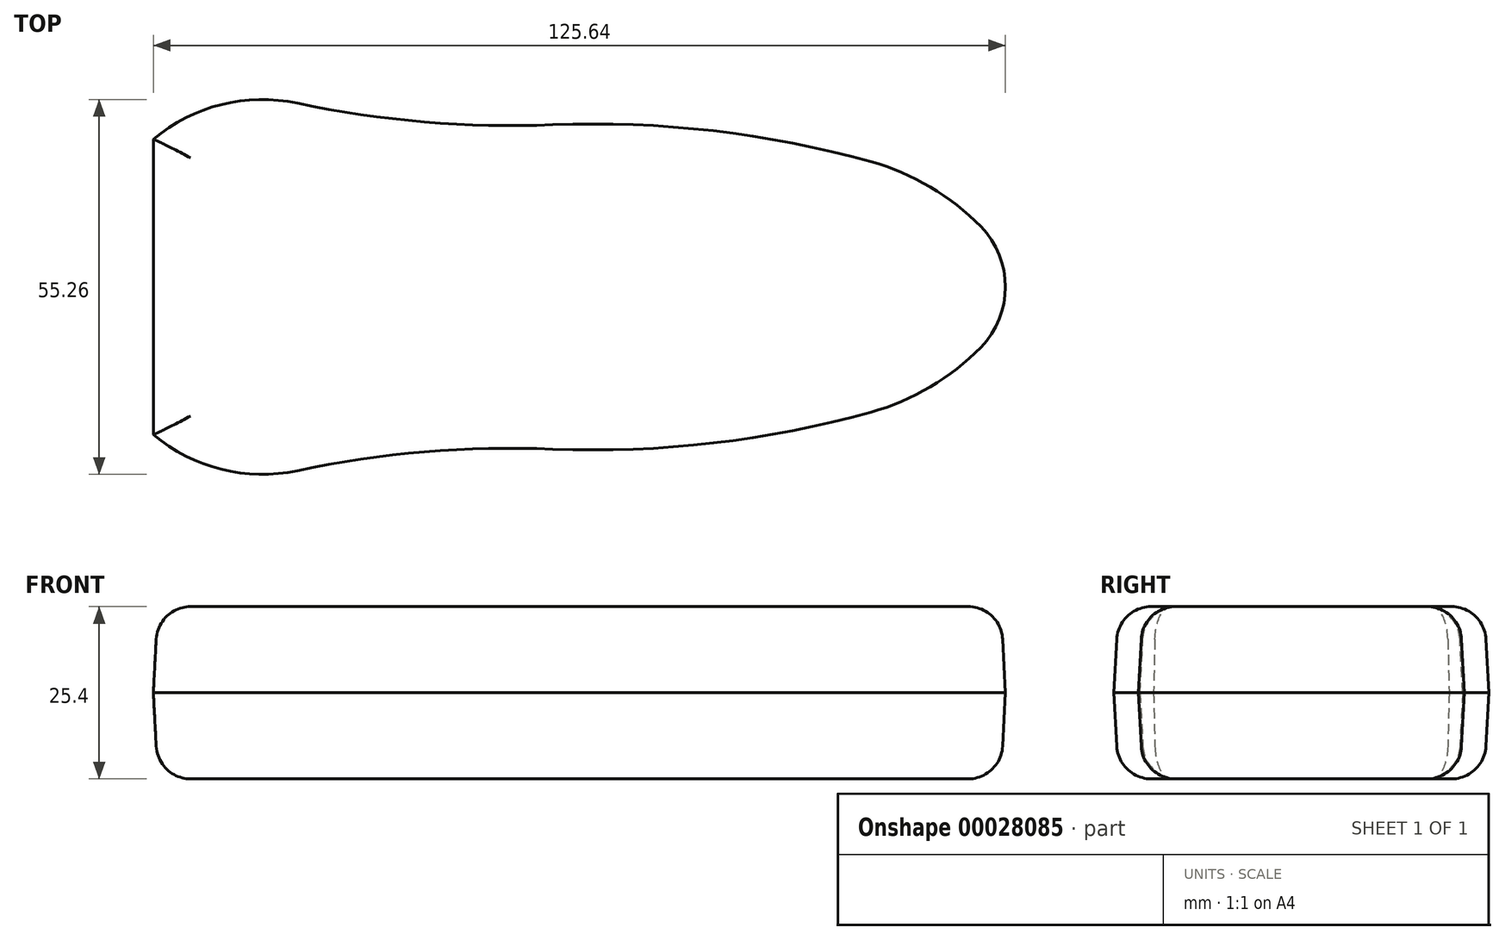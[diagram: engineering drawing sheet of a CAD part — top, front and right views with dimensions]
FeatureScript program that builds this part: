
annotation { "Feature Type Name" : "Feature", "Feature Type Description" : "" }
export const myFeature = defineFeature(function(context is Context, id is Id, definition is map)
    precondition{}
    {
        {
            var Q0;
            Q0=qCreatedBy(makeId("Top.planeOp"),FACE);
            var sketch = newSketch(context, id + "F0", { "sketchPlane" : qUnion([Q0])});
            skArc(sketch, "E0", {"start": v(71.88, 0) * mm, "mid": v(70.94, 4.79) * mm, "end": v(68.27, 8.87) * mm});
            skArc(sketch, "E1", {"start": v(68.27, 8.87) * mm, "mid": v(60.79, 14.74) * mm, "end": v(52.04, 18.47) * mm});
            skPoint(sketch, "E2", {"position": v(71.88, 0) * mm});
            skArc(sketch, "E3", {"start": v(52.04, 18.47) * mm, "mid": v(28.8, 23.02) * mm, "end": v(5.14, 23.9) * mm});
            skArc(sketch, "E4", {"start": v(-32.53, 27.09) * mm, "mid": v(-13.8, 24.33) * mm, "end": v(5.14, 23.9) * mm});
            skLineSegment(sketch, "E5", {"start": v(-53.76, 0) * mm, "end": v(-53.76, 21.8) * mm});
            skArc(sketch, "E6.trimOffspring", {"start": v(-32.53, 27.09) * mm, "mid": v(-43.76, 26.89) * mm, "end": v(-53.76, 21.8) * mm});
            skLineSegment(sketch, "E7", {"start": v(-88.63, 0) * mm, "end": v(102.89, 0) * mm, "construction": true});
            skLineSegment(sketch, "E8.MirrorCS", {"start": v(-53.76, 0) * mm, "end": v(-53.76, -21.8) * mm});
            skArc(sketch, "E9.MirrorCS", {"start": v(-32.53, -27.09) * mm, "mid": v(-43.76, -26.89) * mm, "end": v(-53.76, -21.8) * mm});
            skArc(sketch, "E10.MirrorCS", {"start": v(71.88, 0) * mm, "mid": v(70.94, -4.79) * mm, "end": v(68.27, -8.87) * mm});
            skArc(sketch, "E11.MirrorCS", {"start": v(-32.53, -27.09) * mm, "mid": v(-13.8, -24.33) * mm, "end": v(5.14, -23.9) * mm});
            skArc(sketch, "E12.MirrorCS", {"start": v(52.04, -18.47) * mm, "mid": v(28.8, -23.02) * mm, "end": v(5.14, -23.9) * mm});
            skArc(sketch, "E13.MirrorCS", {"start": v(68.27, -8.87) * mm, "mid": v(60.79, -14.74) * mm, "end": v(52.04, -18.47) * mm});
            skSolve(sketch);
        }
        {
            var Q0;
            Q0=makeQuery(id+"F0.imprint","IMPRINT",FACE,{"disambiguationData":[TD([[makeQuery(id+"F0.imprint","IMPRINT",EDGE,{"derivedFrom":sQuery(id+"F0.wireOp",EDGE,"E0")}),1.0]])]});
            extrude(context, id + "F1", {"entities" : qUnion([Q0]), "depth" : 12.7 * mm, "hasDraft" : true, "draftAngle" : 3 * degree, "draftPullDirection" : true, "hasSecondDirection" : true, "secondDirectionOppositeDirection" : true, "secondDirectionDepth" : 12.7 * mm, "hasSecondDirectionDraft" : true, "secondDirectionDraftAngle" : 3 * degree, "secondDirectionDraftPullDirection" : true});
        }
        {
            var Q0;
            Q0=makeQuery(id+"F1.opExtrude","CAP_FACE",FACE,{"disambiguationData":[OSD([sQuery(id+"F0.wireOp",EDGE,"E0"),sQuery(id+"F0.wireOp",EDGE,"E1"),sQuery(id+"F0.wireOp",EDGE,"E3"),sQuery(id+"F0.wireOp",EDGE,"E4"),sQuery(id+"F0.wireOp",EDGE,"E5"),sQuery(id+"F0.wireOp",EDGE,"E6.trimOffspring"),sQuery(id+"F0.wireOp",EDGE,"E8.MirrorCS"),sQuery(id+"F0.wireOp",EDGE,"E9.MirrorCS"),sQuery(id+"F0.wireOp",EDGE,"E10.MirrorCS"),sQuery(id+"F0.wireOp",EDGE,"E11.MirrorCS"),sQuery(id+"F0.wireOp",EDGE,"E12.MirrorCS"),sQuery(id+"F0.wireOp",EDGE,"E13.MirrorCS")])],"isStart":false});
            fillet(context, id + "F2", {"entities" : qUnion([Q0]), "radius" : 5.08 * mm, "tangentPropagation" : true, "allowEdgeOverflow" : false});
        }
        {
            var Q0;
            Q0=makeQuery(id+"F1.opExtrude","CAP_FACE",FACE,{"disambiguationData":[OSD([sQuery(id+"F0.wireOp",EDGE,"E0"),sQuery(id+"F0.wireOp",EDGE,"E1"),sQuery(id+"F0.wireOp",EDGE,"E3"),sQuery(id+"F0.wireOp",EDGE,"E4"),sQuery(id+"F0.wireOp",EDGE,"E5"),sQuery(id+"F0.wireOp",EDGE,"E6.trimOffspring"),sQuery(id+"F0.wireOp",EDGE,"E8.MirrorCS"),sQuery(id+"F0.wireOp",EDGE,"E9.MirrorCS"),sQuery(id+"F0.wireOp",EDGE,"E10.MirrorCS"),sQuery(id+"F0.wireOp",EDGE,"E11.MirrorCS"),sQuery(id+"F0.wireOp",EDGE,"E12.MirrorCS"),sQuery(id+"F0.wireOp",EDGE,"E13.MirrorCS")])],"isStart":true});
            fillet(context, id + "F3", {"entities" : qUnion([Q0]), "radius" : 5.08 * mm, "tangentPropagation" : true, "allowEdgeOverflow" : false});
        }
    });
